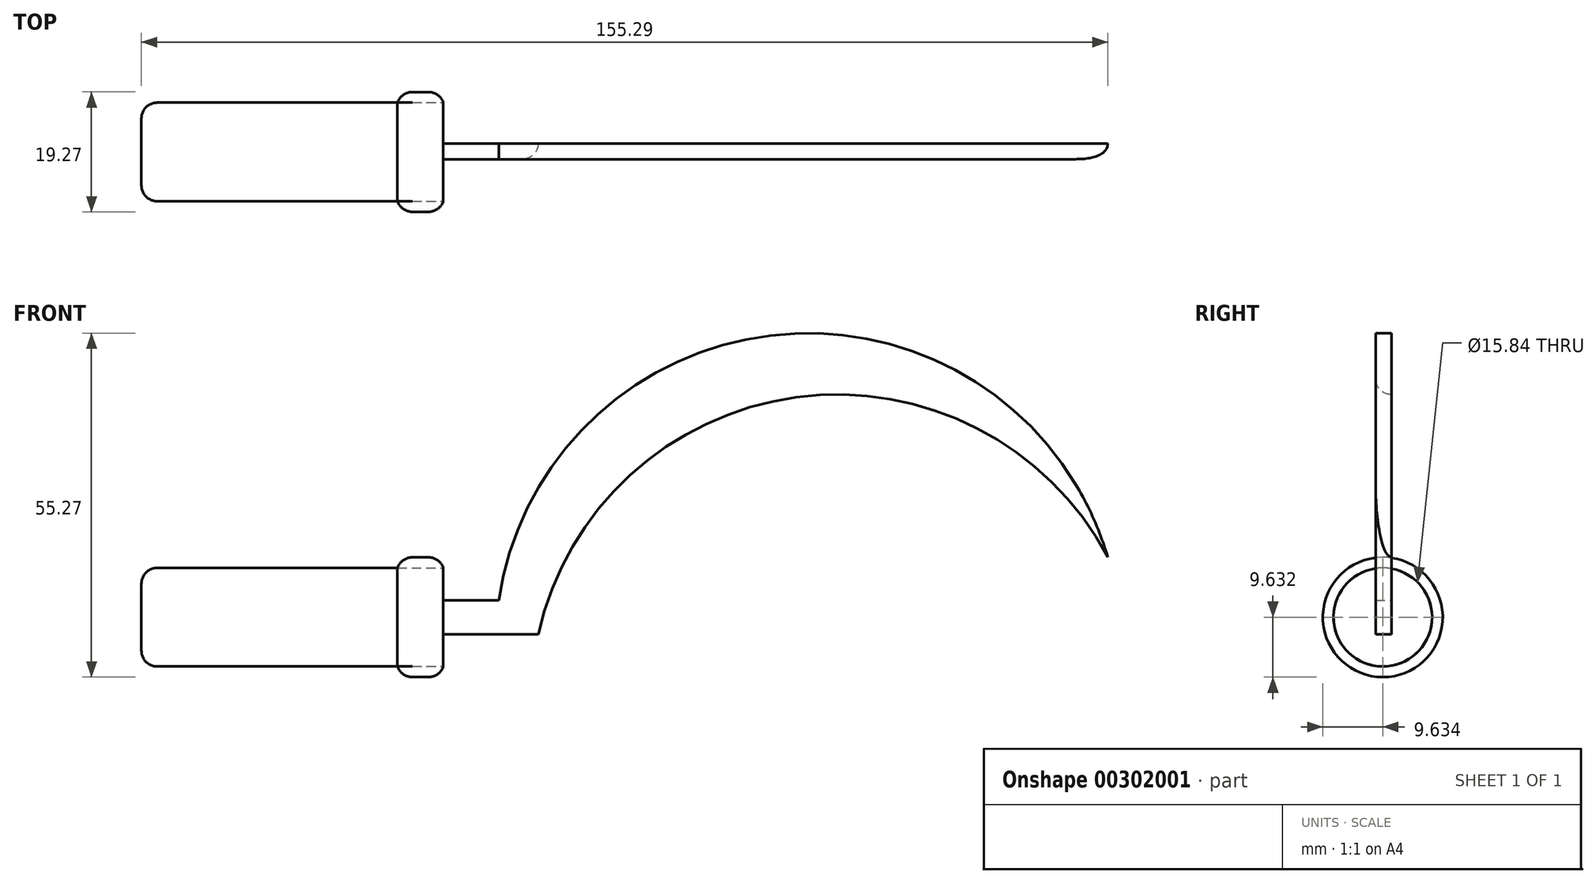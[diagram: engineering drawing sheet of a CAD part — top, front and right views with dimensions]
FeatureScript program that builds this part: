
annotation { "Feature Type Name" : "Feature", "Feature Type Description" : "" }
export const myFeature = defineFeature(function(context is Context, id is Id, definition is map)
    precondition{}
    {
        {
            var Q0;
            Q0=qCreatedBy(makeId("Front.planeOp"),FACE);
            var sketch = newSketch(context, id + "F0", { "sketchPlane" : qUnion([Q0])});
            skArc(sketch, "E0", {"start": v(91.52, -8.35) * mm, "mid": v(39.82, 27.52) * mm, "end": v(-6.33, -15.25) * mm});
            skLineSegment(sketch, "E1", {"start": v(-6.33, -15.25) * mm, "end": v(-15.25, -15.25) * mm});
            skLineSegment(sketch, "E2", {"start": v(-15.25, -15.25) * mm, "end": v(-15.25, -20.72) * mm});
            skLineSegment(sketch, "E3", {"start": v(-15.25, -20.72) * mm, "end": v(0, -20.72) * mm});
            skArc(sketch, "E4", {"start": v(91.52, -8.35) * mm, "mid": v(41.45, 17.35) * mm, "end": v(0, -20.72) * mm});
            skSolve(sketch);
        }
        {
            var Q0;
            Q0=makeQuery(id+"F0.imprint","IMPRINT",FACE,{"disambiguationData":[TD([[makeQuery(id+"F0.imprint","IMPRINT",EDGE,{"derivedFrom":sQuery(id+"F0.wireOp",EDGE,"E0")}),1.0]])]});
            extrude(context, id + "F1", {"entities" : qUnion([Q0]), "depth" : 2.54 * mm});
        }
        {
            var Q0;
            Q0=makeQuery(id+"F1.opExtrude","CAP_EDGE",EDGE,{"disambiguationData":[OSD([sQuery(id+"F0.wireOp",EDGE,"E4")])],"isStart":false});
            fillet(context, id + "F2", {"entities" : qUnion([Q0]), "radius" : 2.54 * mm, "tangentPropagation" : true, "allowEdgeOverflow" : false});
        }
        {
            var Q0;
            Q0=makeQuery(id+"F1.opExtrude","SWEPT_FACE",FACE,{"disambiguationData":[OSD([sQuery(id+"F0.wireOp",EDGE,"E2")])]});
            var sketch = newSketch(context, id + "F3", { "sketchPlane" : qUnion([Q0])});
            skCircle(sketch, "E5", {"center": v(1.38, -17.99) * mm, "radius": 7.92 * mm});
            skPoint(sketch, "E5.centerSnap0", {"position": v(2.54, -17.99) * mm});
            skCircle(sketch, "E6", {"center": v(1.38, -17.99) * mm, "radius": 9.63 * mm});
            skSolve(sketch);
        }
        {
            var Q0;
            Q0=makeQuery(id+"F3.imprint","IMPRINT",FACE,{"disambiguationData":[TD([[makeQuery(id+"F3.imprint","IMPRINT",EDGE,{"derivedFrom":sQuery(id+"F3.wireOp",EDGE,"E5")}),1.0]])]});
            var Q1;
            Q1=sQuery(id+"F3.wireOp",EDGE,"E5");
            extrude(context, id + "F4", {"entities" : qUnion([Q0]), "surfaceEntities" : qUnion([Q1]), "depth" : 48.5 * mm});
        }
        {
            var Q0;
            Q0=makeQuery(id+"F3.imprint","IMPRINT",FACE,{"disambiguationData":[TD([[makeQuery(id+"F3.imprint","IMPRINT",EDGE,{"derivedFrom":sQuery(id+"F3.wireOp",EDGE,"E5")}),-1.0]])]});
            var Q1;
            Q1=sQuery(id+"F3.wireOp",EDGE,"E6");
            extrude(context, id + "F5", {"entities" : qUnion([Q0]), "surfaceEntities" : qUnion([Q1]), "depth" : 7.37 * mm});
        }
        {
            var Q0;
            Q0=makeQuery(id+"F5.opExtrude","CAP_EDGE",EDGE,{"disambiguationData":[OSD([sQuery(id+"F3.wireOp",EDGE,"E6")])],"isStart":false});
            var Q1;
            Q1=makeQuery(id+"F4.opExtrude","CAP_EDGE",EDGE,{"disambiguationData":[OSD([sQuery(id+"F3.wireOp",EDGE,"E5")])],"isStart":false});
            var Q2;
            Q2=makeQuery(id+"F5.opExtrude","CAP_EDGE",EDGE,{"disambiguationData":[OSD([sQuery(id+"F3.wireOp",EDGE,"E6")])],"isStart":true});
            fillet(context, id + "F6", {"entities" : qUnion([Q0, Q1, Q2]), "radius" : 2.54 * mm, "tangentPropagation" : true, "allowEdgeOverflow" : false});
        }
        {
            var Q0;
            {var subQ0=sQuery(id+"F0.wireOp",EDGE,"E2");Q0=makeQuery(id+"F4.opExtrude","SWEPT_FACE",FACE,{"disambiguationData":[OSD([subQ0]),TDD([makeQuery(id+"F3.imprint","IMPRINT",EDGE,{"derivedFrom":makeQuery(id+"F1.opExtrude","CAP_EDGE",EDGE,{"disambiguationData":[OSD([subQ0])],"isStart":true})})])]});}
            var Q1;
            {var subQ0=sQuery(id+"F0.wireOp",EDGE,"E2");Q1=makeQuery(id+"F4.opExtrude","SWEPT_FACE",FACE,{"disambiguationData":[OSD([subQ0]),TDD([makeQuery(id+"F3.imprint","IMPRINT",EDGE,{"derivedFrom":makeQuery(id+"F1.opExtrude","CAP_EDGE",EDGE,{"disambiguationData":[OSD([subQ0])],"isStart":false})})])]});}
            extrude(context, id + "F7", {"entities" : qUnion([Q0]), "operationType" : NewBodyOperationType.ADD, "endBound" : BoundingType.UP_TO_SURFACE, "endBoundEntityFace" : qUnion([Q1]), "depth" : 25.4 * mm});
        }
    });
